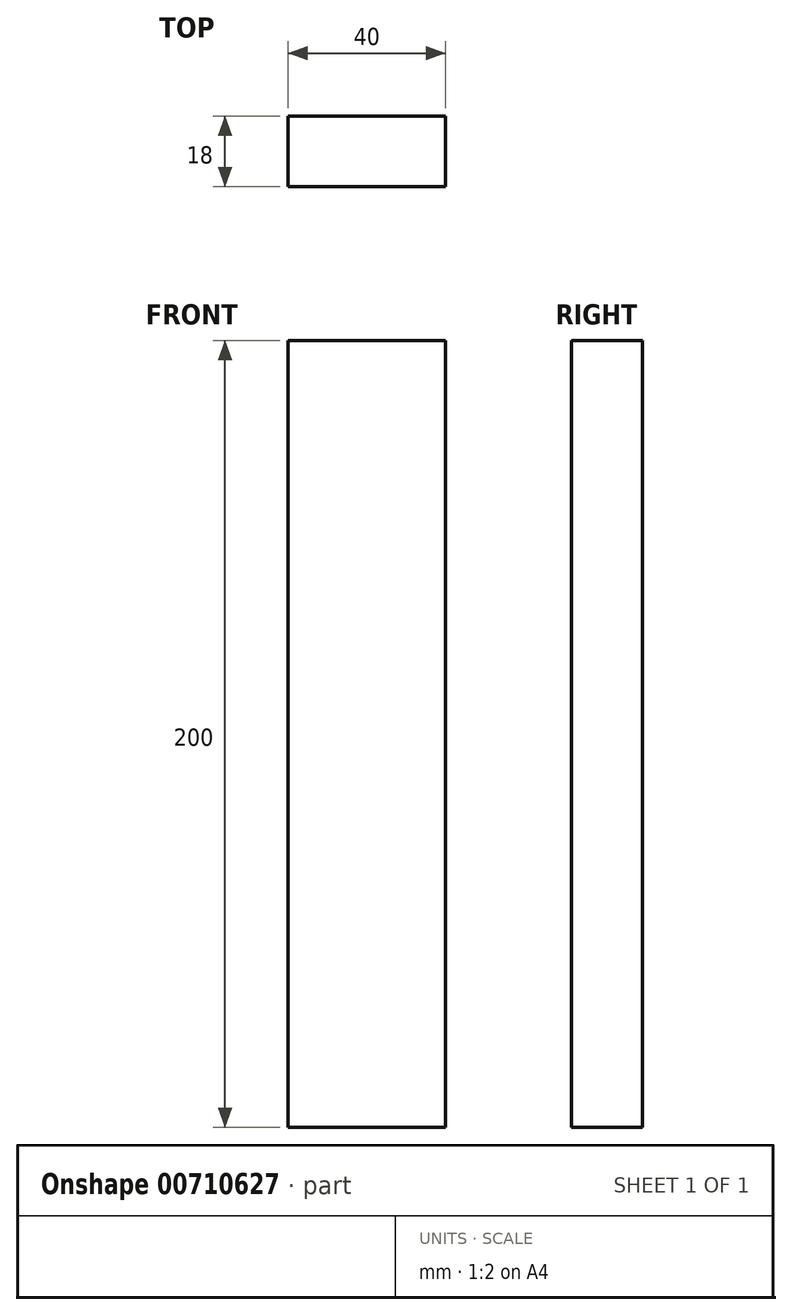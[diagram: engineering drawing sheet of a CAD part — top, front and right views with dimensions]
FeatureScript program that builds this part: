
annotation { "Feature Type Name" : "Feature", "Feature Type Description" : "" }
export const myFeature = defineFeature(function(context is Context, id is Id, definition is map)
    precondition{}
    {
        {
            var Q0;
            Q0=qCreatedBy(makeId("Front.planeOp"),FACE);
            var sketch = newSketch(context, id + "F0", { "sketchPlane" : qUnion([Q0])});
            skLineSegment(sketch, "E0.bottom", {"start": v(0, 0) * mm, "end": v(40, 0) * mm});
            skLineSegment(sketch, "E0.top", {"start": v(0, 200) * mm, "end": v(40, 200) * mm});
            skLineSegment(sketch, "E0.left", {"start": v(0, 0) * mm, "end": v(0, 200) * mm});
            skLineSegment(sketch, "E0.right", {"start": v(40, 0) * mm, "end": v(40, 200) * mm});
            skSolve(sketch);
        }
        {
            var Q0;
            Q0=makeQuery(id+"F0.imprint","IMPRINT",FACE,{"disambiguationData":[TD([[makeQuery(id+"F0.imprint","IMPRINT",EDGE,{"derivedFrom":sQuery(id+"F0.wireOp",EDGE,"E0.bottom")}),1.0]])]});
            extrude(context, id + "F1", {"entities" : qUnion([Q0]), "depth" : 18 * mm, "offsetDistance" : 25 * mm});
        }
    });
